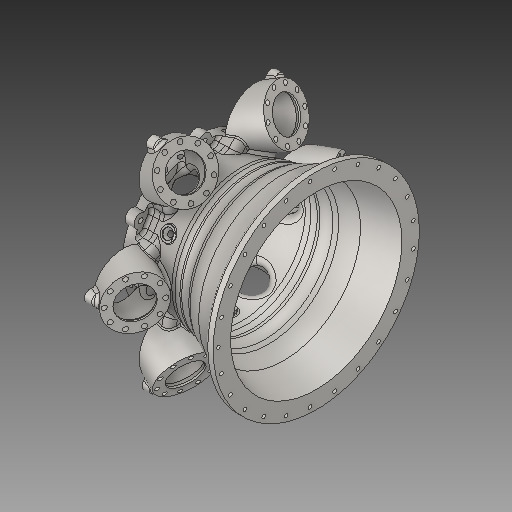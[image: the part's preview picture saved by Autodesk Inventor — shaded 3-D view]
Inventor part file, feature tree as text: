
AUTODESK INVENTOR PART (.ipt)
format: ipt  version: 2019 (Build 230136000, 136)  size: 3,743,232 bytes
history: native  units: mm
features: sketch x19, fillet x16, extrude x10, pattern_circular x9, hole x7, plane x6, other x6, revolve x4, projected_geometry x4, split x1, boolean_combine x1, delete_face x1, chamfer x1, surface_op x1
ambient origin geometry x8: Origin, YZ Plane, XZ Plane, XY Plane, X Axis, Y Axis, Z Axis, Center Point
bodies: Solid2 (feature_tree), Solid4 (feature_tree)
feature tree (86):
  revolve  "Revolution1"  Angle=75.0deg
  fillet  "Fillet1"  Radius=102.0mm
  fillet  "Fillet2"  Radius=20.0mm
  fillet  "Fillet3"  Radius=28.448867mm
  fillet  "Fillet4"  Radius=11.0mm
  extrude  "Extrusion1"  Depth=24.0mm
  extrude  "Extrusion2"  Depth=46.5mm
  sketch  "Sketch4"  dims[d13=90.0deg d15=1.5mm]
  sketch  "Sketch5"  dims[d16=2.9mm d18=7.0mm]
  revolve  "Revolution4"  [1 undecoded]
  extrude  "Extrusion15"  Depth=7.0mm
  revolve  "Revolution5"  [1 undecoded]
  extrude  "Extrusion5"  Depth=61.747mm
  sketch  "Sketch10"  dims[d26=163.0mm d27=9.92mm d28=0.0mm]
  hole  "Hole1"  [1 undecoded]
  pattern_circular  "Circular Pattern4"  Count=12  [1 undecoded]
  extrude  "Extrusion7"  Depth=9.92mm TaperAngle=0.0deg
  pattern_circular  "Circular Pattern2"  [2 undecoded]
  fillet  "Fillet14"  Radius=285.0mm
  fillet  "Fillet15"  [1 undecoded]
  extrude  "Extrusion8"  TaperAngle=90.0deg  [1 undecoded]
  split  "Split3"
  boolean_combine  "Combine3"
  fillet  "Fillet23"  Radius=280.0mm
  fillet  "Fillet22"  Radius=30.0mm
  fillet  "Fillet7"  Radius=60.0mm
  extrude  "Extrusion6"  Depth=2.0mm
  pattern_circular  "Circular Pattern3"  [2 undecoded]
  delete_face  "Delete Face2"
  fillet  "Fillet10"  Radius=100.0mm
  fillet  "Fillet13"  Radius=5.0mm
  pattern_circular  "Circular Pattern5"  [2 undecoded]
  plane  "Work Plane1"
  extrude  "Extrusion9"  Depth=7.0mm
  plane  "Work Plane2"
  extrude  "Extrusion11"  Depth=60.0mm TaperAngle=360.0deg
  hole  "Hole4"  [1 undecoded]
  hole  "Hole5"  [1 undecoded]
  pattern_circular  "Circular Pattern6"  [2 undecoded]
  fillet  "Fillet18"  Radius=0.20944mm
  fillet  "Fillet19"  Radius=5.0mm
  fillet  "Fillet20"  Radius=12.0mm
  sketch  "Sketch18"  dims[d35=5.061455mm]
  plane  "Work Plane3"
  extrude  "Extrusion13"  Depth=10.0mm TaperAngle=0.0deg
  other  "Work Point1"
  pattern_circular  "Circular Pattern7"  [2 undecoded]
  hole  "Hole6"  [1 undecoded]
  fillet  "Fillet21"  Radius=10.188mm
  hole  "Hole7"  [1 undecoded]
  pattern_circular  "Circular Pattern8"  [2 undecoded]
  fillet  "Fillet24"  Radius=3.8mm
  revolve  "Revolution6"  [1 undecoded]
  pattern_circular  "Circular Pattern9"  [2 undecoded]
  plane  "Work Plane6"
  sketch  "Sketch27"  dims[d42=58.0mm d44=52.0mm d46=285.0mm d60=90.0deg d61=90.0deg d62=280.0mm d63=30.0mm d64=15.101mm d65=0.0mm d66=0.0mm d67=60.0mm d68=360.0deg d70=2.0mm d71=27.5mm d72=100.0mm d73=0.0mm d76=5.0mm d78=28.0mm d80=7.0mm d81=60.0mm d82=360.0deg d84=25.0mm d85=5.0mm d86=6.0mm d87=4.0mm d88=2.0mm d89=90.0deg d90=13.061mm d91=0.0mm d92=100.0mm d93=360.0deg d95=132.0mm d96=0.20944mm d97=5.0mm d98=12.0mm d99=10.0mm d100=0.0mm d101=2.0mm d102=3.2mm d103=10.188mm d104=0.0mm d105=60.0mm d106=360.0deg d108=43.5mm d111=3.8mm d112=28.70194mm d113=5.5mm d114=6.0mm d115=3.845mm d116=10.0mm d117=15.5mm d118=2.0mm d119=2.0mm d120=0.0mm d130=2.75mm d131=0.0mm d132=-5.0mm d133=11.0mm d137=5.8mm d139=7.5mm d140=6.5mm d141=0.0mm d143=6.0mm d160=11.34mm d161=6.0mm d162=4.0mm d163=2.0mm d164=90.0deg d165=1.05mm d166=0.0mm d167=6.146mm d168=6.0mm d169=11.34mm d170=2.0mm d171=90.0deg d172=12.0mm d173=0.0mm d174=30.0mm d175=360.0deg d177=8.0mm d178=1.0mm d179=2.0mm d181=15.0mm d182=83.0mm d183=10.0mm d184=8.0mm d185=-10.646508mm d188=10.0mm d189=0.0mm d190=-5.061455mm d195=60.0mm d196=360.0deg d198=5.4mm d199=6.0mm d200=11.34mm d201=2.0mm d202=90.0deg d203=12.0mm d204=0.0mm d205=3.2mm d208=54.0mm d209=69.0mm d210=32.0mm d211=0.0mm d212=8.0mm d213=8.0mm d214=108.0mm d215=4.11mm d216=6.0mm d217=11.34mm d218=2.0mm d219=90.0deg d220=9.0mm d221=0.0mm d222=250.0mm d223=360.0deg d225=3.0mm d226=51.316mm d227=40.723mm d228=16.867mm d229=25.830873mm d230=90.0deg d231=60.0mm d232=360.0deg d235=-7.55mm d236=2.164208mm d237=2.164208mm d262=10.0mm d263=10.0mm d240=5.0mm d241=6.0mm d242=4.0mm d243=2.0mm d244=90.0deg d245=17.0mm d246=0.0mm d264=10.0mm d265=10.0mm d249=5.0mm d250=6.0mm d251=4.0mm d252=2.0mm d253=90.0deg d254=17.0mm d255=0.0mm d256=60.0mm d257=360.0deg d259=1.0mm d260=2.0mm d261=45.0deg]
  other  "Work Axis1"
  other  "Work Axis2"
  other  "Work Point2"
  other  "Work Point3"
  hole  "Hole8"  [1 undecoded]
  hole  "Hole9"  [1 undecoded]
  pattern_circular  "Circular Pattern10"  [2 undecoded]
  chamfer  "Chamfer1"  Distance=15.5mm
  sketch  "Sketch1"  dims[d2=48.5mm d3=75.0deg d4=102.0mm d5=20.0mm d6=28.448867mm d7=11.0mm]
  sketch  "Sketch2"  dims[d8=165.0deg d9=24.0mm]
  sketch  "Sketch3"  dims[d10=133.0mm d12=46.5mm]
  sketch  "Sketch7"  dims[d19=7.0mm d20=1.1mm]
  sketch  "Sketch8"  dims[d21=1.5mm d22=61.747mm]
  projected_geometry  "Projected Loop1"
  sketch  "Sketch9"  dims[d23=20.753mm d24=24.0mm d25=120.0mm]
  sketch  "Sketch11"  dims[d29=227.5mm]
  sketch  "Sketch13"  dims[d30=9.0mm d31=0.0mm]
  sketch  "Sketch16"  dims[d32=86.0mm]
  sketch  "Sketch17"  dims[d33=74.5mm]
  plane  "Work Plane4"
  plane  "Work Plane5"
  sketch  "Sketch21"  dims[d36=11.0mm]
  sketch  "Sketch23"  dims[d37=2.0mm]
  sketch  "Sketch24"  dims[d38=26.354472mm]
  sketch  "Sketch25"  dims[d39=4.5mm]
  surface_op  "Surface2"
  projected_geometry  "Project Cut Edges3"
  other  "Srf2"
  projected_geometry  "Project Cut Edges5"
  projected_geometry  "Project Cut Edges6"
note: 29 required parameter values undecoded (feature->parameter linkage not recoverable at this tier; creation-order binding heuristic only, values carry confidence <= 0.55)